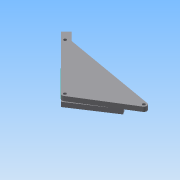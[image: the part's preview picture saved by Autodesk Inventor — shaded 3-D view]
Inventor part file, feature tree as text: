
AUTODESK INVENTOR PART (.ipt)
format: ipt  version: 2015 (Build 190159000, 159)  size: 198,656 bytes
history: native  units: mm
features: extrude x11, sketch x10, other x1, plane x1, mirror x1
ambient origin geometry x8: Origin, YZ Plane, XZ Plane, XY Plane, X Axis, Y Axis, Z Axis, Center Point
bodies: Body1 (feature_tree)
feature tree (24):
  other  "實體1"
  extrude  "擠出1"  Depth=28.86mm
  extrude  "擠出2"  Depth=42.26mm
  sketch  "草圖3"
  extrude  "擠出3"  Depth=25.05mm
  extrude  "擠出4"  Depth=2.5mm
  extrude  "擠出5"  Depth=2.5mm
  extrude  "擠出6"  Depth=2.5mm
  extrude  "擠出7"  Depth=2.0mm TaperAngle=0.0deg
  extrude  "擠出8"  Depth=1.25mm
  extrude  "擠出9"  Depth=1.25mm
  plane  "工作平面1"
  mirror  "鏡射1"
  extrude  "擠出10"  Depth=1.25mm
  extrude  "擠出11"  Depth=2.0mm TaperAngle=0.0deg
  sketch  "草圖1"
  sketch  "草圖2"
  sketch  "草圖4"
  sketch  "草圖5"
  sketch  "草圖6"
  sketch  "草圖7"
  sketch  "草圖8"
  sketch  "草圖9"
  sketch  "草圖10"
